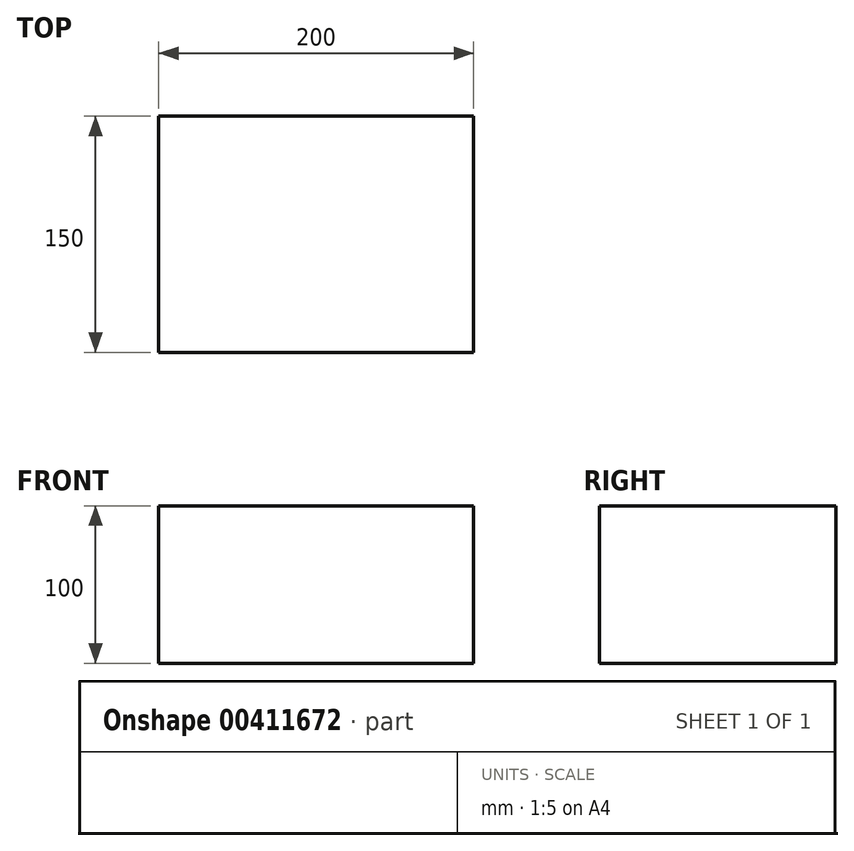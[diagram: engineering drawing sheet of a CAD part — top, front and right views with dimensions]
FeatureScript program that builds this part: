
annotation { "Feature Type Name" : "Feature", "Feature Type Description" : "" }
export const myFeature = defineFeature(function(context is Context, id is Id, definition is map)
    precondition{}
    {
        {
            var Q0;
            Q0=qCreatedBy(makeId("Top.planeOp"),FACE);
            var sketch = newSketch(context, id + "F0", { "sketchPlane" : qUnion([Q0])});
            skLineSegment(sketch, "E0.bottom", {"start": v(100, -75) * mm, "end": v(-100, -75) * mm});
            skLineSegment(sketch, "E0.top", {"start": v(100, 75) * mm, "end": v(-100, 75) * mm});
            skLineSegment(sketch, "E0.left", {"start": v(100, -75) * mm, "end": v(100, 75) * mm});
            skLineSegment(sketch, "E0.right", {"start": v(-100, -75) * mm, "end": v(-100, 75) * mm});
            skPoint(sketch, "E0.middle", {"position": v(0, 0) * mm});
            skSolve(sketch);
        }
        {
            var Q0;
            Q0=makeQuery(id+"F0.imprint","IMPRINT",FACE,{"disambiguationData":[TD([[makeQuery(id+"F0.imprint","IMPRINT",EDGE,{"derivedFrom":sQuery(id+"F0.wireOp",EDGE,"E0.bottom")}),-1.0]])]});
            extrude(context, id + "F1", {"entities" : qUnion([Q0]), "endBound" : BoundingType.SYMMETRIC, "depth" : 100 * mm});
        }
    });
